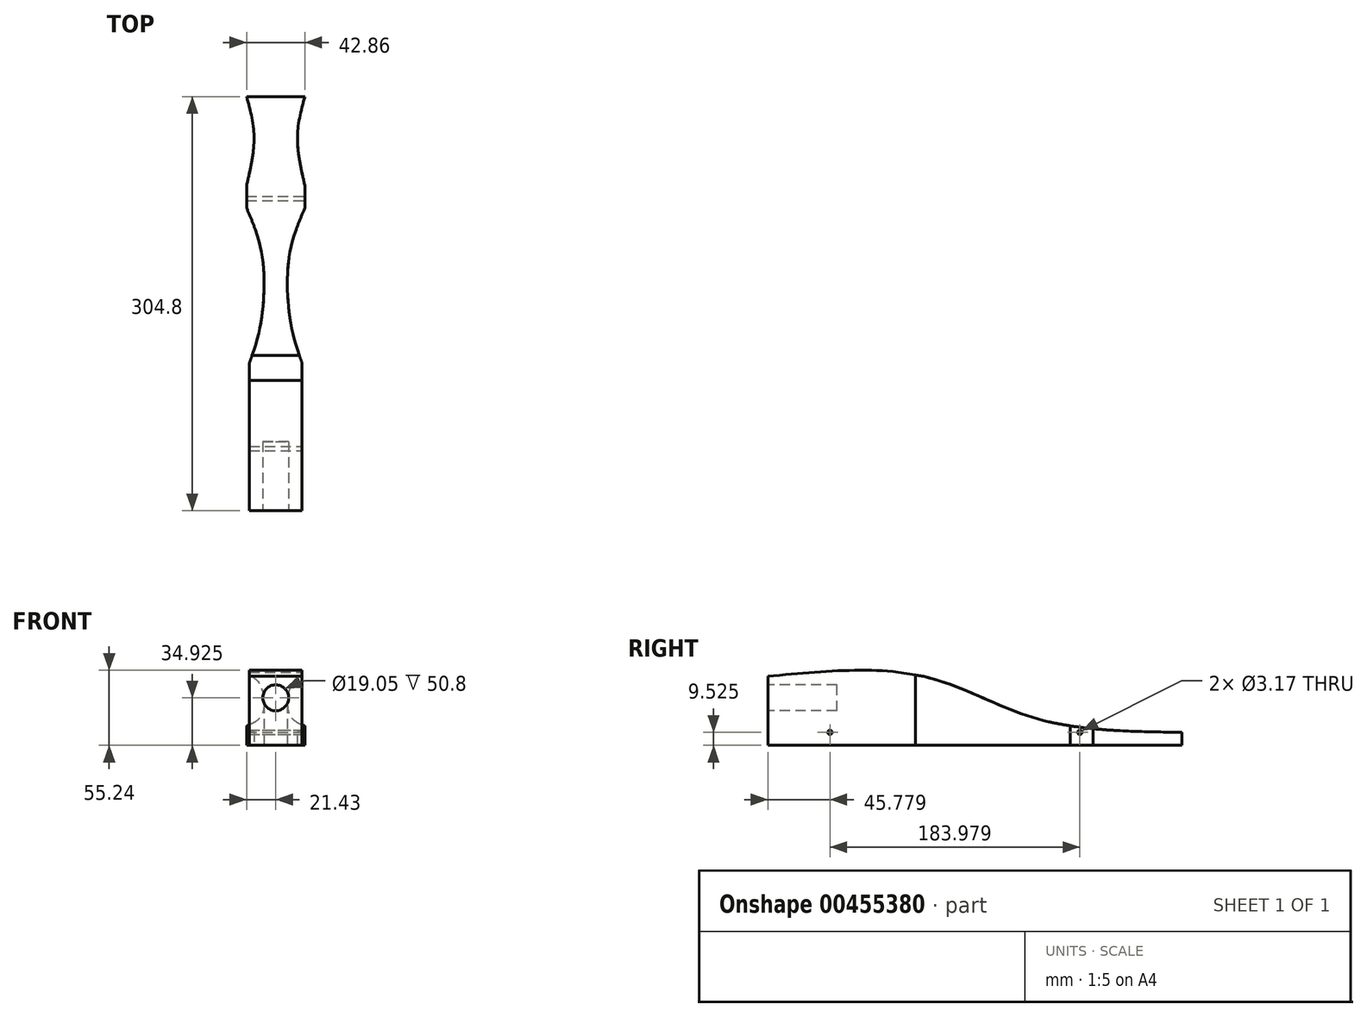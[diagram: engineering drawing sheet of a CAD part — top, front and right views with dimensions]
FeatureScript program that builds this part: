
annotation { "Feature Type Name" : "Feature", "Feature Type Description" : "" }
export const myFeature = defineFeature(function(context is Context, id is Id, definition is map)
    precondition{}
    {
        {
            var Q0;
            Q0=qCreatedBy(makeId("Right.planeOp"),FACE);
            var sketch = newSketch(context, id + "F0", { "sketchPlane" : qUnion([Q0])});
            skLineSegment(sketch, "E0", {"start": v(-152.4, 0) * mm, "end": v(152.4, 0) * mm});
            skLineSegment(sketch, "E1", {"start": v(-152.4, 0) * mm, "end": v(-152.4, 69.85) * mm});
            skLineSegment(sketch, "E2", {"start": v(152.4, 0) * mm, "end": v(152.4, 19.05) * mm});
            skLineSegment(sketch, "E3", {"start": v(152.4, 19.05) * mm, "end": v(-152.4, 69.85) * mm});
            skPoint(sketch, "E4.endSnap0", {"position": v(-152.4, 34.93) * mm});
            skLineSegment(sketch, "E5.0", {"start": v(-95.25, 50.8) * mm, "end": v(-152.4, 50.8) * mm, "construction": true});
            skLineSegment(sketch, "E5.1", {"start": v(-95.25, 50.8) * mm, "end": v(-95.25, 19.05) * mm, "construction": true});
            skLineSegment(sketch, "E5.2", {"start": v(-95.25, 19.05) * mm, "end": v(-152.4, 19.05) * mm, "construction": true});
            skSolve(sketch);
        }
        {
            var Q0;
            Q0=makeQuery(id+"F0.imprint","IMPRINT",FACE,{"disambiguationData":[TD([[makeQuery(id+"F0.imprint","IMPRINT",EDGE,{"derivedFrom":sQuery(id+"F0.wireOp",EDGE,"E0")}),1.0]])]});
            extrude(context, id + "F1", {"entities" : qUnion([Q0]), "depth" : 42.86 * mm, "symmetric" : true});
        }
        {
            var Q0;
            Q0=makeQuery(id+"F1.opExtrude","SWEPT_FACE",FACE,{"disambiguationData":[OSD([sQuery(id+"F0.wireOp",EDGE,"E1")])]});
            var sketch = newSketch(context, id + "F2", { "sketchPlane" : qUnion([Q0])});
            skLineSegment(sketch, "E6", {"start": v(21.43, 34.93) * mm, "end": v(0, 34.93) * mm, "construction": true});
            skCircle(sketch, "E7", {"center": v(0, 34.93) * mm, "radius": 9.53 * mm});
            skSolve(sketch);
        }
        {
            var Q0;
            Q0=makeQuery(id+"F2.imprint","IMPRINT",FACE,{"disambiguationData":[TD([[makeQuery(id+"F2.imprint","IMPRINT",EDGE,{"derivedFrom":sQuery(id+"F2.wireOp",EDGE,"E7")}),1.0]])]});
            var Q1;
            Q1=sQuery(id+"F2.wireOp",EDGE,"E7");
            extrude(context, id + "F3", {"entities" : qUnion([Q0]), "operationType" : NewBodyOperationType.REMOVE, "surfaceEntities" : qUnion([Q1]), "oppositeDirection" : true, "depth" : 50.8 * mm});
        }
        {
            var Q0;
            Q0=makeQuery(id+"F1.opExtrude","CAP_FACE",FACE,{"disambiguationData":[OSD([sQuery(id+"F0.wireOp",EDGE,"E0"),sQuery(id+"F0.wireOp",EDGE,"E1"),sQuery(id+"F0.wireOp",EDGE,"E2"),sQuery(id+"F0.wireOp",EDGE,"E3")])],"isStart":false});
            var sketch = newSketch(context, id + "F4", { "sketchPlane" : qUnion([Q0])});
            skLineSegment(sketch, "E8", {"start": v(-152.4, 34.93) * mm, "end": v(-152.4, 44.45) * mm, "construction": true});
            skLineSegment(sketch, "E9.0", {"start": v(-95.25, 19.05) * mm, "end": v(-152.4, 19.05) * mm, "construction": true});
            skLineSegment(sketch, "E9.1", {"start": v(-95.25, 50.8) * mm, "end": v(-95.25, 19.05) * mm, "construction": true});
            skLineSegment(sketch, "E9.2", {"start": v(-152.4, 50.8) * mm, "end": v(-95.25, 50.8) * mm, "construction": true});
            skLineSegment(sketch, "E10", {"start": v(57.15, 0) * mm, "end": v(57.15, 34.93) * mm, "construction": true});
            skLineSegment(sketch, "E11", {"start": v(-152.4, 44.45) * mm, "end": v(-101.6, 44.45) * mm, "construction": true});
            skLineSegment(sketch, "E12", {"start": v(-101.6, 44.45) * mm, "end": v(-101.6, 25.4) * mm, "construction": true});
            skLineSegment(sketch, "E13", {"start": v(-101.6, 25.4) * mm, "end": v(-152.4, 25.4) * mm, "construction": true});
            skFitSpline(sketch, "E14", {"points": [v(-152.4, 50.8) * mm, v(-38.1, 50.8) * mm, v(44.66, 19.9) * mm, v(152.4, 9.53) * mm], "startDerivative": vector(345.38, 32.92) * mm, "endDerivative": vector(332.7, -4.42) * mm});
            skCircle(sketch, "E15", {"center": v(-106.62, 9.53) * mm, "radius": 1.59 * mm});
            skCircle(sketch, "E16", {"center": v(77.36, 9.53) * mm, "radius": 1.59 * mm});
            skFitSpline(sketch, "E17", {"points": [v(106.91, 10.72) * mm, v(90.71, 14.47) * mm, v(76.92, 17.62) * mm, v(69.9, 17.13) * mm, v(54.58, 17.3) * mm], "startDerivative": vector(-56.9, 12.05) * mm, "endDerivative": vector(-62.9, 3.58) * mm});
            skSolve(sketch);
        }
        {
            var Q0;
            Q0=makeQuery(id+"F1.opExtrude","SWEPT_FACE",FACE,{"disambiguationData":[OSD([sQuery(id+"F0.wireOp",EDGE,"E0")])]});
            var sketch = newSketch(context, id + "F5", { "sketchPlane" : qUnion([Q0])});
            skLineSegment(sketch, "E18", {"start": v(0, 152.4) * mm, "end": v(0, -152.4) * mm, "construction": true});
            skLineSegment(sketch, "E19", {"start": v(21.43, -57.15) * mm, "end": v(-21.43, -57.15) * mm, "construction": true});
            skLineSegment(sketch, "E20", {"start": v(15.88, 152.4) * mm, "end": v(15.88, 95.25) * mm, "construction": true});
            skLineSegment(sketch, "E21", {"start": v(15.88, 95.25) * mm, "end": v(-15.87, 95.25) * mm, "construction": true});
            skLineSegment(sketch, "E22", {"start": v(-15.87, 95.25) * mm, "end": v(-15.87, 152.4) * mm, "construction": true});
            skLineSegment(sketch, "E23", {"start": v(0, 152.4) * mm, "end": v(-9.53, 152.4) * mm, "construction": true});
            skLineSegment(sketch, "E24", {"start": v(-9.53, 152.4) * mm, "end": v(-9.53, 101.6) * mm, "construction": true});
            skLineSegment(sketch, "E25", {"start": v(-9.52, 101.6) * mm, "end": v(9.53, 101.6) * mm, "construction": true});
            skLineSegment(sketch, "E26", {"start": v(9.53, 101.6) * mm, "end": v(9.53, 152.4) * mm, "construction": true});
            skLineSegment(sketch, "E27", {"start": v(-19.38, 152.4) * mm, "end": v(-19.38, 43.57) * mm});
            skFitSpline(sketch, "E28", {"points": [v(-19.38, 43.57) * mm, v(-11.37, 16.23) * mm, v(-9.92, -34.6) * mm, v(-21.43, -70.42) * mm], "startDerivative": vector(31.1, -85.15) * mm, "endDerivative": vector(-42.88, -99.96) * mm});
            skFitSpline(sketch, "E29", {"points": [v(-21.43, -87.18) * mm, v(-15.98, -122.5) * mm, v(-21.43, -152.4) * mm], "startDerivative": vector(16.15, -69.36) * mm, "endDerivative": vector(-16.6, -60.97) * mm});
            skFitSpline(sketch, "E30.MirrorCS", {"points": [v(21.43, -87.18) * mm, v(15.98, -122.5) * mm, v(21.43, -152.4) * mm], "startDerivative": vector(-16.15, -69.36) * mm, "endDerivative": vector(16.6, -60.97) * mm});
            skFitSpline(sketch, "E31.MirrorCS", {"points": [v(19.38, 43.57) * mm, v(11.37, 16.23) * mm, v(9.92, -34.6) * mm, v(21.43, -70.42) * mm], "startDerivative": vector(-31.1, -85.15) * mm, "endDerivative": vector(42.88, -99.96) * mm});
            skLineSegment(sketch, "E32.MirrorCS", {"start": v(19.38, 152.4) * mm, "end": v(19.38, 43.57) * mm});
            skSolve(sketch);
        }
        {
            var Q0;
            Q0=makeQuery(id+"F4.imprint","IMPRINT",FACE,{"disambiguationData":[TD([[makeQuery(id+"F4.imprint","IMPRINT",EDGE,{"derivedFrom":sQuery(id+"F4.wireOp",EDGE,"E15")}),-1.0]])]});
            extrude(context, id + "F6", {"entities" : qUnion([Q0]), "operationType" : NewBodyOperationType.INTERSECT, "endBound" : BoundingType.THROUGH_ALL, "oppositeDirection" : true, "depth" : 25.4 * mm});
        }
        {
            var Q0;
            {var subQ5=sQuery(id+"F5.wireOp",EDGE,"E27");Q0=makeQuery(id+"F5.imprint","IMPRINT",FACE,{"disambiguationData":[TD([[makeQuery(id+"F5.imprint","IMPRINT",EDGE,{"derivedFrom":subQ5}),1.0]])]});}
            extrude(context, id + "F7", {"entities" : qUnion([Q0]), "operationType" : NewBodyOperationType.INTERSECT, "endBound" : BoundingType.THROUGH_ALL, "oppositeDirection" : true, "depth" : 25.4 * mm});
        }
    });
